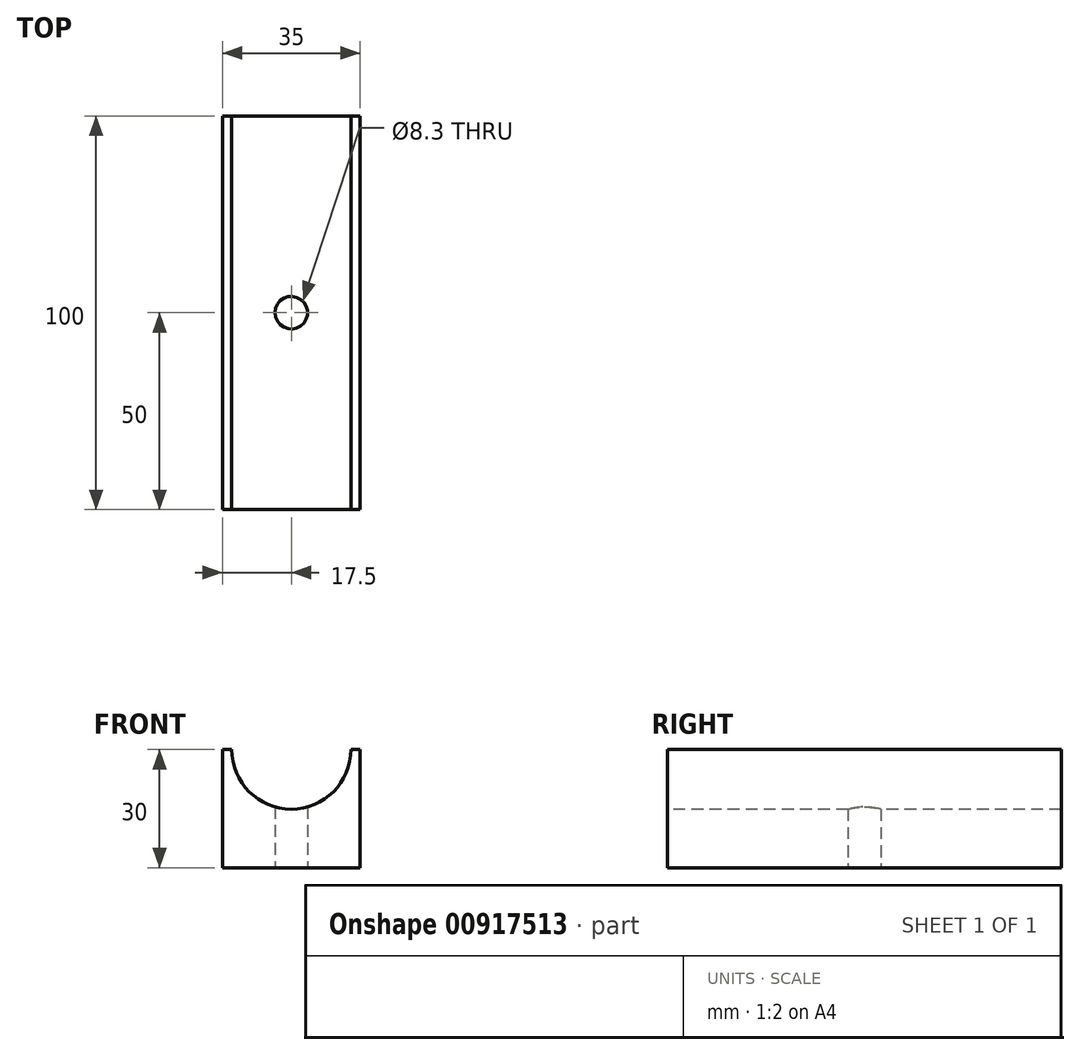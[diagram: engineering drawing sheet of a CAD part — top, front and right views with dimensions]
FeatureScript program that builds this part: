
annotation { "Feature Type Name" : "Feature", "Feature Type Description" : "" }
export const myFeature = defineFeature(function(context is Context, id is Id, definition is map)
    precondition{}
    {
        {
            var Q0;
            Q0=qCreatedBy(makeId("Top.planeOp"),FACE);
            var sketch = newSketch(context, id + "F0", { "sketchPlane" : qUnion([Q0])});
            skLineSegment(sketch, "E0.bottom", {"start": v(0, 0) * mm, "end": v(35, 0) * mm});
            skLineSegment(sketch, "E0.top", {"start": v(0, 100) * mm, "end": v(35, 100) * mm});
            skLineSegment(sketch, "E0.left", {"start": v(0, 0) * mm, "end": v(0, 100) * mm});
            skLineSegment(sketch, "E0.right", {"start": v(35, 0) * mm, "end": v(35, 100) * mm});
            skSolve(sketch);
        }
        {
            var Q0;
            Q0 = qSketchRegion(id + "F0", true);
            extrude(context, id + "F1", {"entities" : qUnion([Q0]), "depth" : 30 * mm, "offsetDistance" : 25 * mm});
        }
        {
            var Q0;
            Q0=makeQuery(id+"F1.opExtrude","SWEPT_FACE",FACE,{"disambiguationData":[OSD([sQuery(id+"F0.wireOp",EDGE,"E0.bottom")])]});
            var sketch = newSketch(context, id + "F2", { "sketchPlane" : qUnion([Q0])});
            skCircle(sketch, "E1", {"center": v(17.5, 30) * mm, "radius": 15.15 * mm});
            skSolve(sketch);
        }
        {
            var Q0;
            Q0 = qSketchRegion(id + "F2", true);
            extrude(context, id + "F3", {"entities" : qUnion([Q0]), "operationType" : NewBodyOperationType.REMOVE, "oppositeDirection" : true, "depth" : 999 * mm, "offsetDistance" : 25 * mm});
        }
        {
            var Q0;
            Q0=makeQuery(id+"F1.opExtrude","CAP_FACE",FACE,{"disambiguationData":[OSD([sQuery(id+"F0.wireOp",EDGE,"E0.bottom"),sQuery(id+"F0.wireOp",EDGE,"E0.top"),sQuery(id+"F0.wireOp",EDGE,"E0.left"),sQuery(id+"F0.wireOp",EDGE,"E0.right")])],"isStart":true});
            var sketch = newSketch(context, id + "F4", { "sketchPlane" : qUnion([Q0])});
            skLineSegment(sketch, "E2", {"start": v(17.5, 0) * mm, "end": v(17.5, -100) * mm, "construction": true});
            skLineSegment(sketch, "E3", {"start": v(0, -50) * mm, "end": v(35, -50) * mm, "construction": true});
            skCircle(sketch, "E4", {"center": v(17.5, -50) * mm, "radius": 4.15 * mm});
            skSolve(sketch);
        }
        {
            var Q0;
            Q0 = qSketchRegion(id + "F4", true);
            extrude(context, id + "F5", {"entities" : qUnion([Q0]), "operationType" : NewBodyOperationType.REMOVE, "oppositeDirection" : true, "depth" : 25 * mm, "offsetDistance" : 25 * mm});
        }
    });
